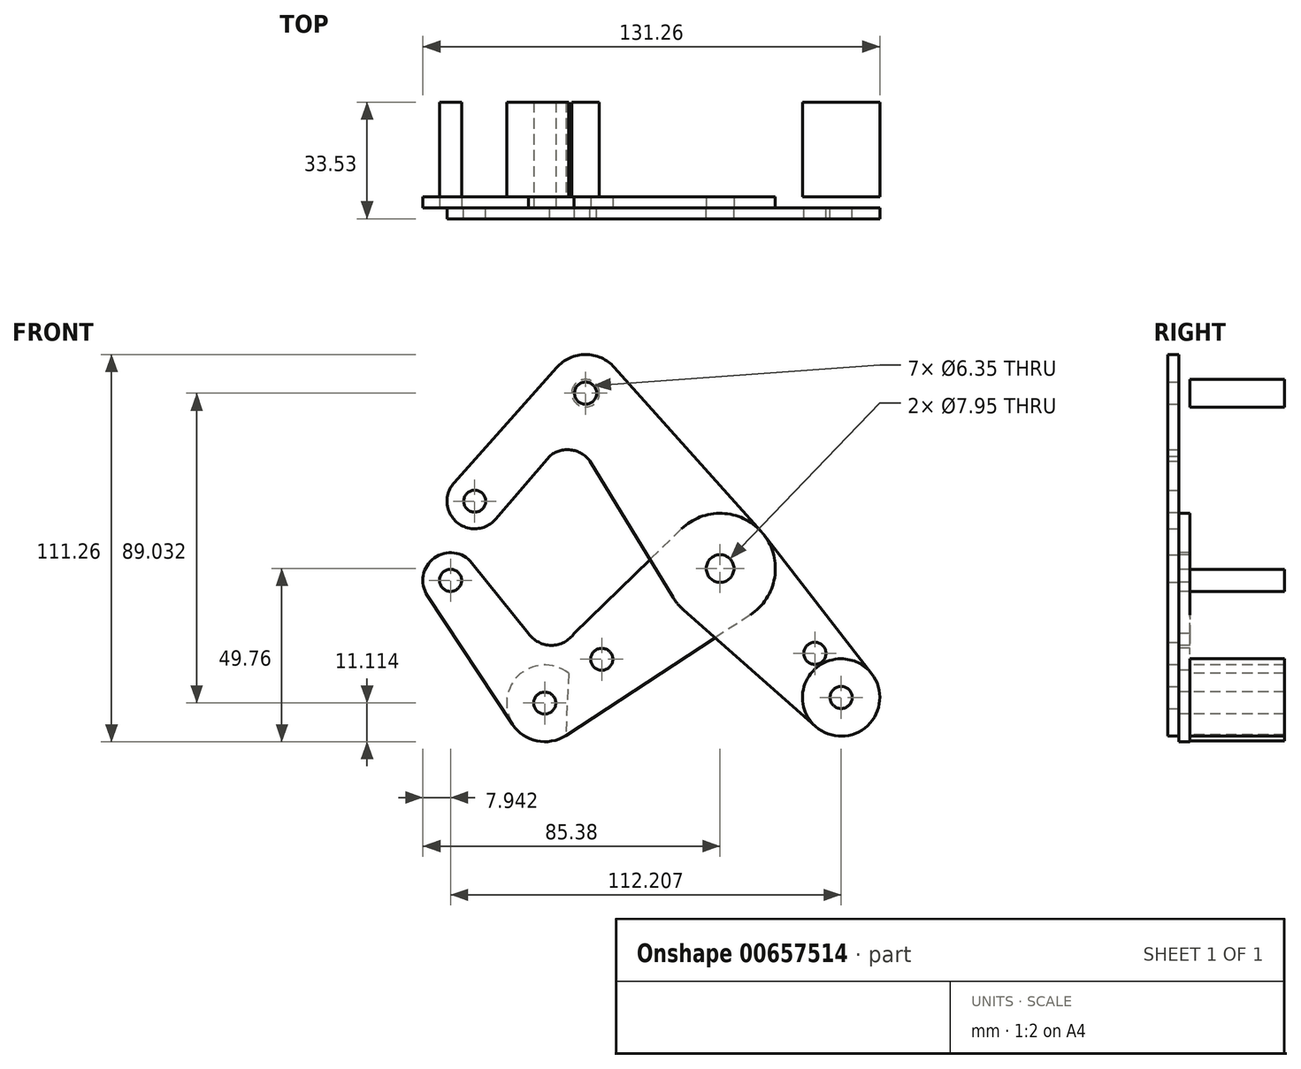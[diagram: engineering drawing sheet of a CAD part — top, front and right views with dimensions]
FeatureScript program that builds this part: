
annotation { "Feature Type Name" : "Feature", "Feature Type Description" : "" }
export const myFeature = defineFeature(function(context is Context, id is Id, definition is map)
    precondition{}
    {
        {
            var Q0;
            Q0=qCreatedBy(makeId("Front.planeOp"),FACE);
            var sketch = newSketch(context, id + "F0", { "sketchPlane" : qUnion([Q0])});
            skCircle(sketch, "E0", {"center": v(0, 0) * mm, "radius": 3.98 * mm});
            skCircle(sketch, "E1", {"center": v(0, 0) * mm, "radius": 15.88 * mm});
            skCircle(sketch, "E2", {"center": v(-38.65, 50.39) * mm, "radius": 11.11 * mm});
            skCircle(sketch, "E3", {"center": v(-38.65, 50.39) * mm, "radius": 3.18 * mm});
            skCircle(sketch, "E4", {"center": v(-70.49, 19.37) * mm, "radius": 3.18 * mm});
            skCircle(sketch, "E5", {"center": v(-70.49, 19.37) * mm, "radius": 7.94 * mm});
            skCircle(sketch, "E6", {"center": v(0, 0) * mm, "radius": 3.18 * mm});
            skCircle(sketch, "E7", {"center": v(34.77, -37.04) * mm, "radius": 3.18 * mm});
            skCircle(sketch, "E8", {"center": v(34.77, -37.04) * mm, "radius": 11.11 * mm});
            skLineSegment(sketch, "E9", {"start": v(-38.65, 50.39) * mm, "end": v(-70.49, 19.37) * mm, "construction": true});
            skLineSegment(sketch, "E10", {"start": v(-38.65, 50.39) * mm, "end": v(0, 0) * mm, "construction": true});
            skLineSegment(sketch, "E11", {"start": v(0, 0) * mm, "end": v(34.77, -37.04) * mm, "construction": true});
            skCircle(sketch, "E12", {"center": v(27.22, -24.36) * mm, "radius": 3.18 * mm});
            skLineSegment(sketch, "E13", {"start": v(0, 0) * mm, "end": v(-50.39, -38.65) * mm, "construction": true});
            skCircle(sketch, "E14", {"center": v(-50.39, -38.65) * mm, "radius": 11.11 * mm});
            skCircle(sketch, "E15", {"center": v(-50.39, -38.65) * mm, "radius": 3.18 * mm});
            skCircle(sketch, "E16", {"center": v(-34, -26.08) * mm, "radius": 3.18 * mm});
            skLineSegment(sketch, "E17", {"start": v(-50.39, -38.65) * mm, "end": v(-77.44, -3.38) * mm, "construction": true});
            skCircle(sketch, "E18", {"center": v(-77.44, -3.38) * mm, "radius": 3.18 * mm});
            skCircle(sketch, "E19", {"center": v(-77.44, -3.38) * mm, "radius": 7.94 * mm});
            skLineSegment(sketch, "E20", {"start": v(-30.36, 57.8) * mm, "end": v(11.84, 10.58) * mm});
            skLineSegment(sketch, "E21", {"start": v(12.54, 9.73) * mm, "end": v(43.55, -30.22) * mm});
            skLineSegment(sketch, "E22", {"start": v(-10.5, -11.9) * mm, "end": v(27.42, -45.37) * mm});
            skLineSegment(sketch, "E23", {"start": v(-46.95, 57.77) * mm, "end": v(-76.42, 24.65) * mm});
            skLineSegment(sketch, "E24", {"start": v(-84.07, -7.74) * mm, "end": v(-59.66, -44.76) * mm});
            skLineSegment(sketch, "E25", {"start": v(8.69, -13.29) * mm, "end": v(-44.3, -47.95) * mm});
            skArc(sketch, "E26", {"start": v(-49, 32.25) * mm, "mid": v(-42.92, 34.1) * mm, "end": v(-37.42, 30.91) * mm});
            skLineSegment(sketch, "E27", {"start": v(-13.56, -8.26) * mm, "end": v(-37.42, 30.91) * mm});
            skLineSegment(sketch, "E28", {"start": v(-49, 32.25) * mm, "end": v(-64.46, 14.2) * mm});
            skArc(sketch, "E29", {"start": v(-41.92, -18.6) * mm, "mid": v(-48.48, -22.05) * mm, "end": v(-55.03, -18.6) * mm});
            skLineSegment(sketch, "E30", {"start": v(-11.07, 11.38) * mm, "end": v(-41.92, -18.6) * mm});
            skLineSegment(sketch, "E31", {"start": v(-55.03, -18.6) * mm, "end": v(-71.25, 1.6) * mm});
            skLineSegment(sketch, "E32", {"start": v(-70.49, 19.37) * mm, "end": v(-77.44, -3.38) * mm, "construction": true});
            skSolve(sketch);
        }
        {
            var Q0;
            Q0=makeQuery(id+"F0.imprint","IMPRINT",FACE,{"disambiguationData":[TD([[makeQuery(id+"F0.imprint","IMPRINT",EDGE,{"derivedFrom":sQuery(id+"F0.wireOp",EDGE,"E0")}),-1.0]])]});
            var Q1;
            Q1=makeQuery(id+"F0.imprint","IMPRINT",FACE,{"disambiguationData":[TD([[makeQuery(id+"F0.imprint","IMPRINT",EDGE,{"derivedFrom":sQuery(id+"F0.wireOp",EDGE,"E12")}),-1.0]])]});
            var Q2;
            Q2=makeQuery(id+"F0.imprint","IMPRINT",FACE,{"disambiguationData":[TD([[makeQuery(id+"F0.imprint","IMPRINT",EDGE,{"derivedFrom":sQuery(id+"F0.wireOp",EDGE,"E7")}),-1.0]])]});
            var Q3;
            {var subQ0=sQuery(id+"F0.wireOp",EDGE,"E20");Q3=makeQuery(id+"F0.imprint","IMPRINT",FACE,{"disambiguationData":[TD([[makeQuery(id+"F0.imprint","IMPRINT",EDGE,{"derivedFrom":subQ0}),-1.0]])]});}
            var Q4;
            Q4=makeQuery(id+"F0.imprint","IMPRINT",FACE,{"disambiguationData":[TD([[makeQuery(id+"F0.imprint","IMPRINT",EDGE,{"derivedFrom":sQuery(id+"F0.wireOp",EDGE,"E3")}),-1.0]])]});
            var Q5;
            Q5=makeQuery(id+"F0.imprint","IMPRINT",FACE,{"disambiguationData":[TD([[makeQuery(id+"F0.imprint","IMPRINT",EDGE,{"derivedFrom":sQuery(id+"F0.wireOp",EDGE,"E4")}),-1.0]])]});
            var Q6;
            {var subQ0=sQuery(id+"F0.wireOp",EDGE,"E22");var subQ1=sQuery(id+"F0.wireOp",EDGE,"E1");var subQ2=makeQuery(id+"F0.imprint","INTERSECT",VERTEX,{"derivedFrom":[subQ1,subQ0]});Q6=makeQuery(id+"F0.imprint","IMPRINT",FACE,{"disambiguationData":[TD([[makeQuery(id+"F0.imprint","IMPRINT",EDGE,{"disambiguationData":[TD([[subQ2,-1.0]])],"derivedFrom":subQ1}),-1.0]])]});}
            var Q7;
            {var subQ0=sQuery(id+"F0.wireOp",EDGE,"E27");var subQ1=sQuery(id+"F0.wireOp",EDGE,"E1");var subQ2=makeQuery(id+"F0.imprint","INTERSECT",VERTEX,{"derivedFrom":[subQ1,subQ0]});Q7=makeQuery(id+"F0.imprint","IMPRINT",FACE,{"disambiguationData":[TD([[makeQuery(id+"F0.imprint","IMPRINT",EDGE,{"disambiguationData":[TD([[subQ2,1.0]])],"derivedFrom":subQ1}),-1.0]])]});}
            extrude(context, id + "F1", {"entities" : qUnion([Q0, Q1, Q2, Q3, Q4, Q5, Q6, Q7]), "depth" : 3.17 * mm, "offsetDistance" : 25.4 * mm});
        }
        {
            var Q0;
            Q0=makeQuery(id+"F0.imprint","IMPRINT",FACE,{"disambiguationData":[TD([[makeQuery(id+"F0.imprint","IMPRINT",EDGE,{"derivedFrom":sQuery(id+"F0.wireOp",EDGE,"E16")}),-1.0]])]});
            var Q1;
            Q1=makeQuery(id+"F0.imprint","IMPRINT",FACE,{"disambiguationData":[TD([[makeQuery(id+"F0.imprint","IMPRINT",EDGE,{"derivedFrom":sQuery(id+"F0.wireOp",EDGE,"E18")}),-1.0]])]});
            var Q2;
            Q2=makeQuery(id+"F0.imprint","IMPRINT",FACE,{"disambiguationData":[TD([[makeQuery(id+"F0.imprint","IMPRINT",EDGE,{"derivedFrom":sQuery(id+"F0.wireOp",EDGE,"E15")}),-1.0]])]});
            var Q3;
            Q3=makeQuery(id+"F0.imprint","IMPRINT",FACE,{"disambiguationData":[TD([[makeQuery(id+"F0.imprint","IMPRINT",EDGE,{"derivedFrom":sQuery(id+"F0.wireOp",EDGE,"E0")}),-1.0]])]});
            var Q4;
            {var subQ0=sQuery(id+"F0.wireOp",EDGE,"E22");var subQ1=sQuery(id+"F0.wireOp",EDGE,"E1");var subQ2=makeQuery(id+"F0.imprint","INTERSECT",VERTEX,{"derivedFrom":[subQ1,subQ0]});Q4=makeQuery(id+"F0.imprint","IMPRINT",FACE,{"disambiguationData":[TD([[makeQuery(id+"F0.imprint","IMPRINT",EDGE,{"disambiguationData":[TD([[subQ2,-1.0]])],"derivedFrom":subQ1}),-1.0]])]});}
            var Q5;
            {var subQ0=sQuery(id+"F0.wireOp",EDGE,"E27");var subQ1=sQuery(id+"F0.wireOp",EDGE,"E1");var subQ2=makeQuery(id+"F0.imprint","INTERSECT",VERTEX,{"derivedFrom":[subQ1,subQ0]});Q5=makeQuery(id+"F0.imprint","IMPRINT",FACE,{"disambiguationData":[TD([[makeQuery(id+"F0.imprint","IMPRINT",EDGE,{"disambiguationData":[TD([[subQ2,1.0]])],"derivedFrom":subQ1}),-1.0]])]});}
            extrude(context, id + "F2", {"entities" : qUnion([Q0, Q1, Q2, Q3, Q4, Q5]), "depth" : -3.17 * mm, "offsetDistance" : 25.4 * mm});
        }
        {
            var Q0;
            Q0=makeQuery(id+"F2.opExtrude","CAP_FACE",FACE,{"disambiguationData":[OSD([sQuery(id+"F0.wireOp",EDGE,"E0"),sQuery(id+"F0.wireOp",EDGE,"E1"),sQuery(id+"F0.wireOp",EDGE,"E14"),sQuery(id+"F0.wireOp",EDGE,"E15"),sQuery(id+"F0.wireOp",EDGE,"E16"),sQuery(id+"F0.wireOp",EDGE,"E18"),sQuery(id+"F0.wireOp",EDGE,"E19"),sQuery(id+"F0.wireOp",EDGE,"E24"),sQuery(id+"F0.wireOp",EDGE,"E25"),sQuery(id+"F0.wireOp",EDGE,"E29"),sQuery(id+"F0.wireOp",EDGE,"E30"),sQuery(id+"F0.wireOp",EDGE,"E31")])],"isStart":false});
            var sketch = newSketch(context, id + "F3", { "sketchPlane" : qUnion([Q0])});
            skCircle(sketch, "E33", {"center": v(38.65, 50.39) * mm, "radius": 3.98 * mm});
            skCircle(sketch, "E34", {"center": v(0, 0) * mm, "radius": 3.98 * mm});
            skCircle(sketch, "E35", {"center": v(-34.77, -37.04) * mm, "radius": 11.11 * mm});
            skLineSegment(sketch, "E36", {"start": v(53.12, -37.04) * mm, "end": v(-34.77, -37.04) * mm, "construction": true});
            skArc(sketch, "E37", {"start": v(44.3, -47.71) * mm, "mid": v(61.3, -38.19) * mm, "end": v(43.55, -30.12) * mm});
            skLineSegment(sketch, "E38", {"start": v(43.55, -30.12) * mm, "end": v(44.3, -47.95) * mm});
            skSolve(sketch);
        }
        {
            var Q0;
            {var subQ0=sQuery(id+"F3.wireOp",EDGE,"E37");Q0=makeQuery(id+"F3.imprint","IMPRINT",FACE,{"disambiguationData":[TD([[makeQuery(id+"F3.imprint","IMPRINT",EDGE,{"derivedFrom":subQ0}),1.0]])]});}
            var Q1;
            Q1=makeQuery(id+"F3.imprint","IMPRINT",FACE,{"disambiguationData":[TD([[makeQuery(id+"F3.imprint","IMPRINT",EDGE,{"derivedFrom":sQuery(id+"F3.wireOp",EDGE,"E33")}),1.0]])]});
            var Q2;
            Q2=makeQuery(id+"F3.imprint","IMPRINT",FACE,{"disambiguationData":[TD([[makeQuery(id+"F3.imprint","IMPRINT",EDGE,{"derivedFrom":makeQuery(id+"F2.opExtrude","CAP_EDGE",EDGE,{"disambiguationData":[OSD([sQuery(id+"F0.wireOp",EDGE,"E18")])],"isStart":false})}),-1.0]])]});
            var Q3;
            Q3=makeQuery(id+"F3.imprint","IMPRINT",FACE,{"disambiguationData":[TD([[makeQuery(id+"F3.imprint","IMPRINT",EDGE,{"derivedFrom":sQuery(id+"F3.wireOp",EDGE,"E35")}),1.0]])]});
            extrude(context, id + "F4", {"entities" : qUnion([Q0, Q1, Q2, Q3]), "operationType" : NewBodyOperationType.ADD, "depth" : 27.18 * mm, "offsetDistance" : 25.4 * mm});
        }
    });
